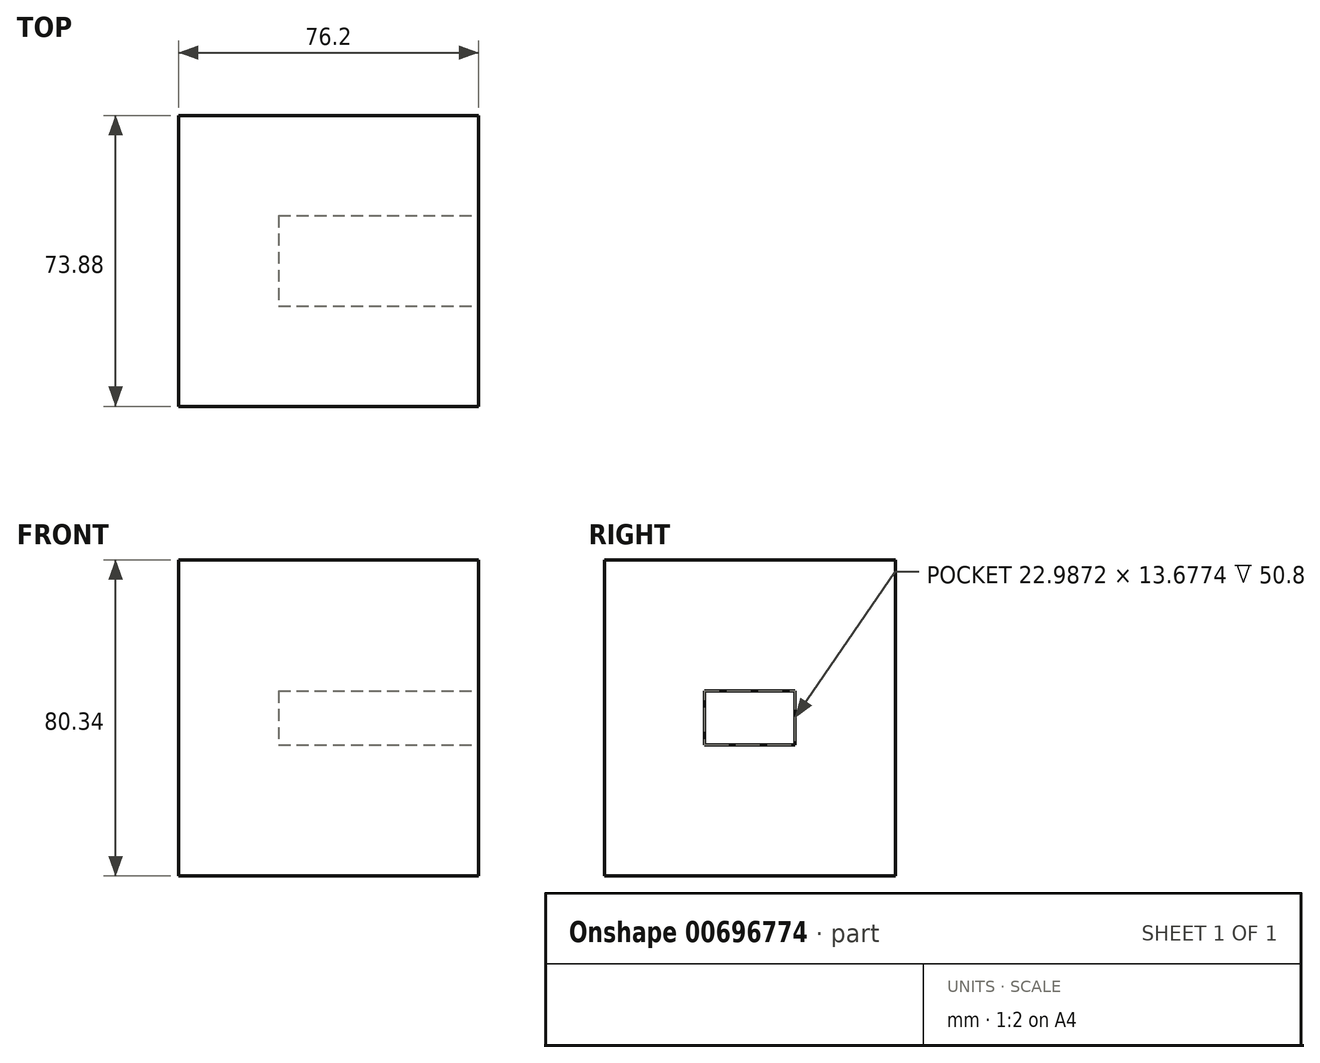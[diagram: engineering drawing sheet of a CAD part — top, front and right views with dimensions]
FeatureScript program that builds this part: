
annotation { "Feature Type Name" : "Feature", "Feature Type Description" : "" }
export const myFeature = defineFeature(function(context is Context, id is Id, definition is map)
    precondition{}
    {
        {
            var Q0;
            Q0=qCreatedBy(makeId("Right.planeOp"),FACE);
            var sketch = newSketch(context, id + "F0", { "sketchPlane" : qUnion([Q0])});
            skLineSegment(sketch, "E0.bottom", {"start": v(36.94, 40.17) * mm, "end": v(-36.94, 40.17) * mm});
            skLineSegment(sketch, "E0.top", {"start": v(36.94, -40.17) * mm, "end": v(-36.94, -40.17) * mm});
            skLineSegment(sketch, "E0.left", {"start": v(36.94, 40.17) * mm, "end": v(36.94, -40.17) * mm});
            skLineSegment(sketch, "E0.right", {"start": v(-36.94, 40.17) * mm, "end": v(-36.94, -40.17) * mm});
            skPoint(sketch, "E0.middle", {"position": v(0, 0) * mm});
            skSolve(sketch);
        }
        {
            var Q0;
            Q0=qSketchRegion(id+"F0",true);
            extrude(context, id + "F1", {"entities" : qUnion([Q0]), "oppositeDirection" : true, "depth" : 76.2 * mm, "offsetDistance" : 25.4 * mm});
        }
        {
            var Q0;
            Q0=makeQuery(id+"F1.opExtrude","CAP_FACE",FACE,{"disambiguationData":[OSD([sQuery(id+"F0.wireOp",EDGE,"E0.bottom"),sQuery(id+"F0.wireOp",EDGE,"E0.top"),sQuery(id+"F0.wireOp",EDGE,"E0.left"),sQuery(id+"F0.wireOp",EDGE,"E0.right")])],"isStart":true});
            var sketch = newSketch(context, id + "F2", { "sketchPlane" : qUnion([Q0])});
            skLineSegment(sketch, "E1.bottom", {"start": v(11.5, 6.84) * mm, "end": v(-11.5, 6.84) * mm});
            skLineSegment(sketch, "E1.top", {"start": v(11.5, -6.84) * mm, "end": v(-11.5, -6.84) * mm});
            skLineSegment(sketch, "E1.left", {"start": v(11.5, 6.84) * mm, "end": v(11.5, -6.84) * mm});
            skLineSegment(sketch, "E1.right", {"start": v(-11.5, 6.84) * mm, "end": v(-11.5, -6.84) * mm});
            skPoint(sketch, "E1.middle", {"position": v(0, 0) * mm});
            skSolve(sketch);
        }
        {
            var Q0;
            Q0=makeQuery(id+"F2.imprint","IMPRINT",FACE,{"disambiguationData":[TD([[makeQuery(id+"F2.imprint","IMPRINT",EDGE,{"derivedFrom":sQuery(id+"F2.wireOp",EDGE,"E1.bottom")}),1.0]])]});
            extrude(context, id + "F3", {"entities" : qUnion([Q0]), "operationType" : NewBodyOperationType.REMOVE, "oppositeDirection" : true, "depth" : 50.8 * mm, "offsetDistance" : 25.4 * mm});
        }
    });
